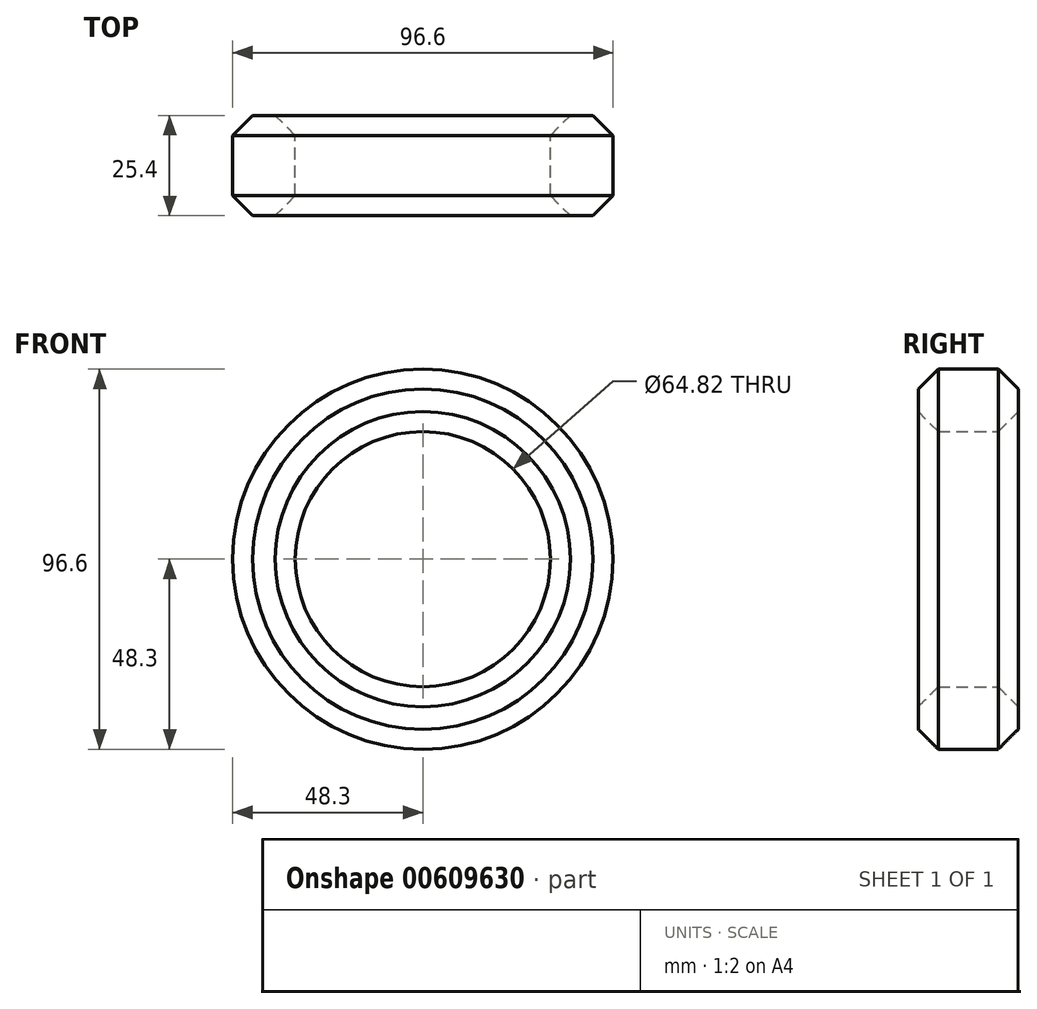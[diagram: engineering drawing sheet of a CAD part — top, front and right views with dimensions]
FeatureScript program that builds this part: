
annotation { "Feature Type Name" : "Feature", "Feature Type Description" : "" }
export const myFeature = defineFeature(function(context is Context, id is Id, definition is map)
    precondition{}
    {
        {
            var Q0;
            Q0=qCreatedBy(makeId("Front.planeOp"),FACE);
            var sketch = newSketch(context, id + "F0", { "sketchPlane" : qUnion([Q0])});
            skCircle(sketch, "E0", {"center": v(0, 0) * mm, "radius": 48.3 * mm});
            skCircle(sketch, "E1", {"center": v(0, 0) * mm, "radius": 32.41 * mm});
            skSolve(sketch);
        }
        {
            var Q0;
            Q0 = qSketchRegion(id + "F0", true);
            extrude(context, id + "F1", {"entities" : qUnion([Q0]), "depth" : 25.4 * mm, "offsetDistance" : 25.4 * mm});
        }
        {
            var Q0;
            Q0=makeQuery(id+"F1.opExtrude","CAP_EDGE",EDGE,{"disambiguationData":[OSD([sQuery(id+"F0.wireOp",EDGE,"E0")])],"isStart":false});
            var Q1;
            Q1=makeQuery(id+"F1.opExtrude","CAP_FACE",FACE,{"disambiguationData":[OSD([sQuery(id+"F0.wireOp",EDGE,"E0"),sQuery(id+"F0.wireOp",EDGE,"E1")])],"isStart":true});
            var Q2;
            Q2=makeQuery(id+"F1.opExtrude","SWEPT_FACE",FACE,{"disambiguationData":[OSD([sQuery(id+"F0.wireOp",EDGE,"E1")])]});
            chamfer(context, id + "F2", {"entities" : qUnion([Q0, Q1, Q2]), "width" : 5.08 * mm, "tangentPropagation" : true});
        }
    });
